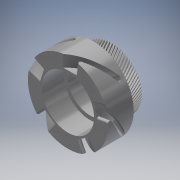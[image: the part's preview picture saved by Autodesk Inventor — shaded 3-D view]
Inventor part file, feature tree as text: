
AUTODESK INVENTOR PART (.ipt)
format: ipt  version: 2017 (Build 210142000, 142)  size: 1,509,376 bytes
history: native  units: mm (DEFAULTED — no unit token found)
features: sketch x7, extrude x5, plane x3, other x3, fillet x2, projected_geometry x2, helix x1, pattern_circular x1
ambient origin geometry x8: Origin, YZ Plane, XZ Plane, XY Plane, X Axis, Y Axis, Z Axis, Center Point
bodies: Solid1 (feature_tree)
feature tree (24):
  extrude  "Extrusion1"  Depth=12.7mm TaperAngle=0.0deg
  plane  "Work Plane1"
  plane  "Work Plane2"
  plane  "Work Plane3"
  other  "Spur Gear"
  extrude  "Extrusion2"  Depth=76.2mm TaperAngle=0.0deg
  extrude  "Extrusion3"  TaperAngle=0.0deg  [1 undecoded]
  extrude  "Extrusion4"  TaperAngle=0.0deg  [1 undecoded]
  helix  "Coil1"  [1 undecoded]
  fillet  "Fillet1"  Radius=69.342mm
  fillet  "Fillet2"  Radius=45.212mm
  pattern_circular  "Circular Pattern1"  [2 undecoded]
  extrude  "Extrusion5"  Depth=3.81mm
  sketch  "Sketch1"  dims[d0=51.854614mm d1=12.7mm d2=0.0mm]
  sketch  "Sketch2"  dims[d3=50.947674mm d4=76.2mm d5=0.0mm]
  other  "Srf1"
  sketch  "Sketch3"  dims[d6=0.0mm d7=0.455303mm d9=0.0mm]
  sketch  "Sketch4"  dims[d14=0.0mm d15=31.75mm d16=0.0mm d17=0.0mm d18=0.0mm d19=31.75mm d20=69.342mm d21=45.212mm]
  sketch  "Sketch5"  dims[d22=25.4mm d23=0.0mm]
  projected_geometry  "Projected Loop1"
  sketch  "Sketch6"  dims[d24=38.354mm]
  projected_geometry  "Projected Loop2"
  sketch  "Sketch7"  dims[d25=50.8mm d26=0.0mm d27=6.35mm d28=0.0mm d29=3.81mm d30=3.81mm d31=127.0mm d32=19.05mm d33=5.0mm d34=0.0mm d35=90.0deg d36=90.0deg d37=0.0mm d38=0.0mm d39=1.5875mm d40=1.5875mm d41=50.0mm d42=360.0deg d44=24.13mm d45=25.4mm d46=8.255mm d47=3.175mm d48=0.0mm]
  other  "Pitch Diameter"
note: 5 required parameter values undecoded (feature->parameter linkage not recoverable at this tier; creation-order binding heuristic only, values carry confidence <= 0.55)
